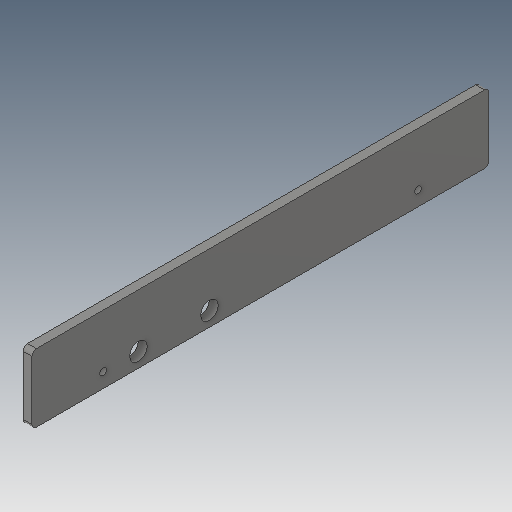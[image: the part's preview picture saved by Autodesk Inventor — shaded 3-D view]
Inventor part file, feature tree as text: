
AUTODESK INVENTOR PART (.ipt)
format: ipt  version: 2023.5 (Build 275446000, 446)  size: 92,672 bytes
history: native  units: in
note: dims shown in document units (in); Inventor stores cm internally (conversion verified against a paired STEP export)
features: fillet x1
ambient origin geometry x8: Origin, YZ Plane, XZ Plane, XY Plane, X Axis, Y Axis, Z Axis, Center Point
bodies: Solid1 (feature_tree)
feature tree (1):
  fillet  "Fillet1"  [1 undecoded]
note: 1 required parameter value undecoded (feature->parameter linkage not recoverable at this tier; creation-order binding heuristic only, values carry confidence <= 0.55)
